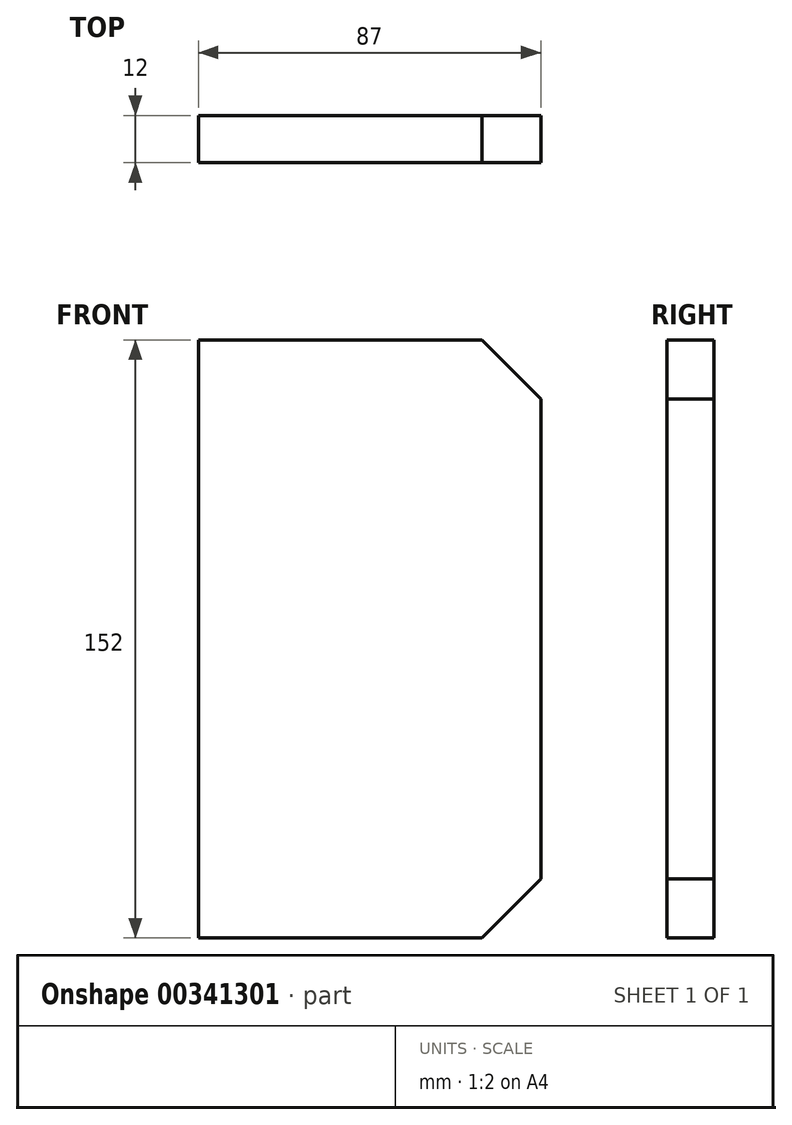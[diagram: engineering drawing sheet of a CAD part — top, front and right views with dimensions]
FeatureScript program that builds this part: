
annotation { "Feature Type Name" : "Feature", "Feature Type Description" : "" }
export const myFeature = defineFeature(function(context is Context, id is Id, definition is map)
    precondition{}
    {
        {
            var Q0;
            Q0=qCreatedBy(makeId("Front.planeOp"),FACE);
            var sketch = newSketch(context, id + "F0", { "sketchPlane" : qUnion([Q0])});
            skLineSegment(sketch, "E0.bottom", {"start": v(0, 0) * mm, "end": v(87, 0) * mm});
            skLineSegment(sketch, "E0.top", {"start": v(0, 152) * mm, "end": v(87, 152) * mm});
            skLineSegment(sketch, "E0.left", {"start": v(0, 0) * mm, "end": v(0, 152) * mm});
            skLineSegment(sketch, "E0.right", {"start": v(87, 0) * mm, "end": v(87, 152) * mm});
            skSolve(sketch);
        }
        {
            var Q0;
            Q0=makeQuery(id+"F0.imprint","IMPRINT",FACE,{"disambiguationData":[TD([[makeQuery(id+"F0.imprint","IMPRINT",EDGE,{"derivedFrom":sQuery(id+"F0.wireOp",EDGE,"E0.bottom")}),1.0]])]});
            extrude(context, id + "F1", {"entities" : qUnion([Q0]), "depth" : 12 * mm});
        }
        {
            var Q0;
            Q0=makeQuery(id+"F1.opExtrude","SWEPT_EDGE",EDGE,{"disambiguationData":[OSD([sQuery(id+"F0.wireOp",EDGE,"E0.top"),sQuery(id+"F0.wireOp",EDGE,"E0.right")])]});
            var Q1;
            Q1=makeQuery(id+"F1.opExtrude","SWEPT_EDGE",EDGE,{"disambiguationData":[OSD([sQuery(id+"F0.wireOp",EDGE,"E0.bottom"),sQuery(id+"F0.wireOp",EDGE,"E0.right")])]});
            chamfer(context, id + "F2", {"entities" : qUnion([Q0, Q1]), "width" : 15 * mm, "tangentPropagation" : true});
        }
    });
